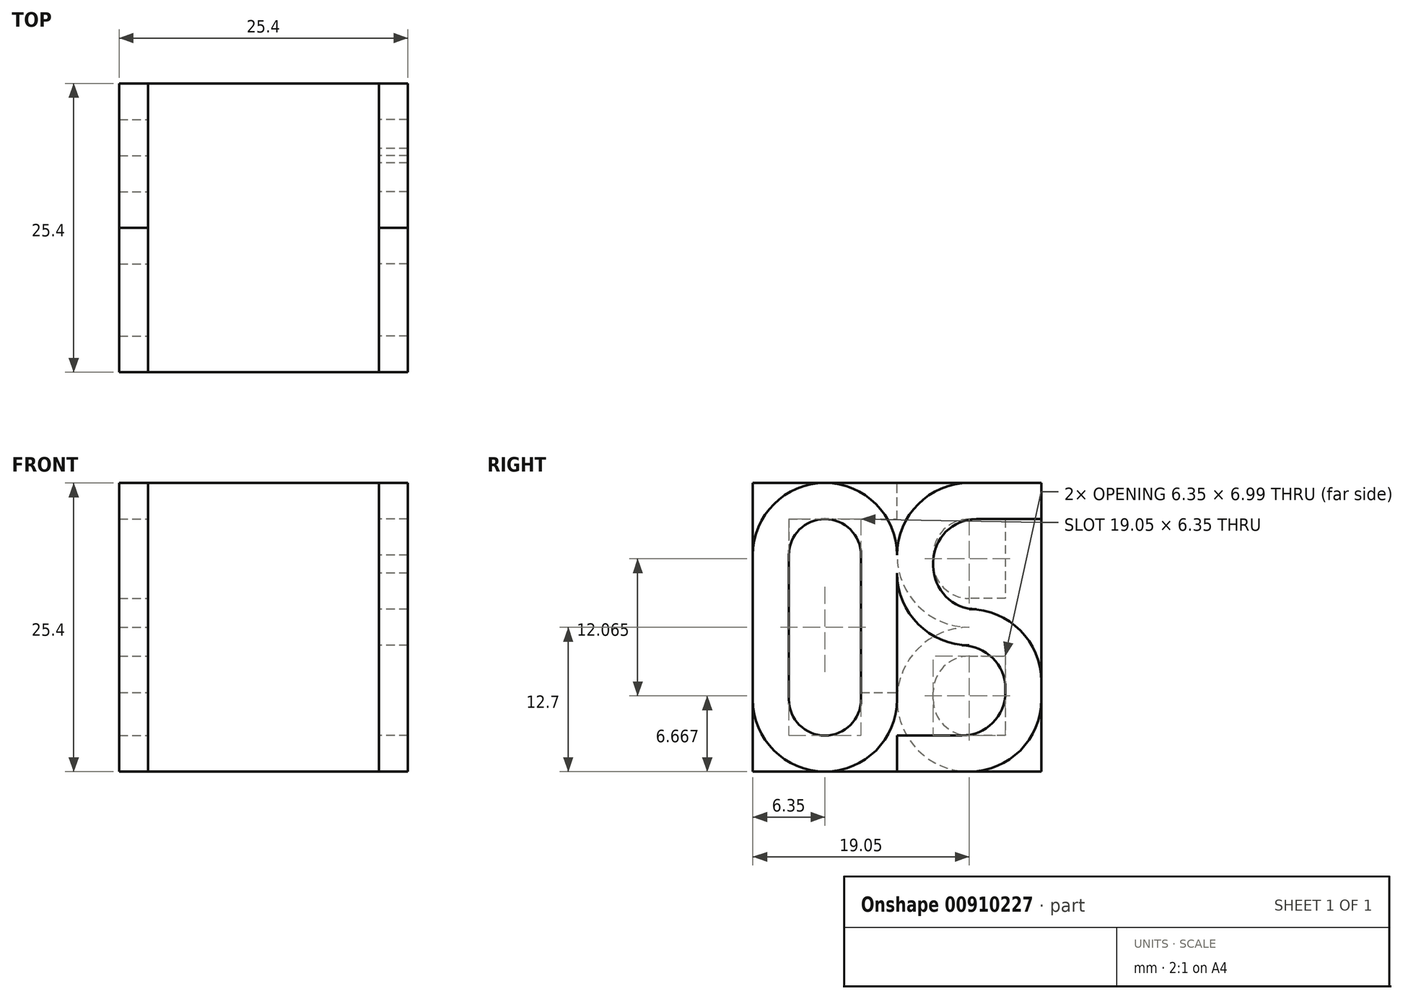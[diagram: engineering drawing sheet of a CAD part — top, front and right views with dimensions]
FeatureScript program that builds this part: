
annotation { "Feature Type Name" : "Feature", "Feature Type Description" : "" }
export const myFeature = defineFeature(function(context is Context, id is Id, definition is map)
    precondition{}
    {
        {
            var Q0;
            Q0=qCreatedBy(makeId("Right.planeOp"),FACE);
            var sketch = newSketch(context, id + "F0", { "sketchPlane" : qUnion([Q0])});
            skLineSegment(sketch, "E0.bottom", {"start": v(11.43, 12.7) * mm, "end": v(6.35, 12.7) * mm});
            skLineSegment(sketch, "E0.top", {"start": v(6.35, -12.7) * mm, "end": v(1.27, -12.7) * mm});
            skLineSegment(sketch, "E0.right", {"start": v(-12.7, 6.35) * mm, "end": v(-12.7, -6.35) * mm});
            skPoint(sketch, "E0.middle", {"position": v(0, 0) * mm});
            skLineSegment(sketch, "E1.bottom", {"start": v(-6.35, 12.7) * mm, "end": v(-6.35, 12.7) * mm});
            skLineSegment(sketch, "E1.right", {"start": v(0, 6.35) * mm, "end": v(0, 4.76) * mm});
            skLineSegment(sketch, "E2.bottom", {"start": v(-6.35, 9.53) * mm, "end": v(-6.35, 9.53) * mm});
            skLineSegment(sketch, "E2.top", {"start": v(-6.35, -9.53) * mm, "end": v(-6.35, -9.53) * mm});
            skLineSegment(sketch, "E2.left", {"start": v(-3.17, 6.35) * mm, "end": v(-3.17, -6.35) * mm});
            skLineSegment(sketch, "E2.right", {"start": v(-9.53, 6.35) * mm, "end": v(-9.53, -6.35) * mm});
            skLineSegment(sketch, "E3", {"start": v(11.43, 9.53) * mm, "end": v(6.98, 9.53) * mm});
            skLineSegment(sketch, "E4", {"start": v(3.18, 5.71) * mm, "end": v(3.18, 5.4) * mm});
            skLineSegment(sketch, "E5", {"start": v(6.35, 1.59) * mm, "end": v(6.98, 1.59) * mm});
            skLineSegment(sketch, "E6", {"start": v(12.7, -4.76) * mm, "end": v(12.7, -6.35) * mm});
            skLineSegment(sketch, "E7", {"start": v(1.27, -9.52) * mm, "end": v(5.72, -9.52) * mm});
            skLineSegment(sketch, "E8", {"start": v(9.53, -5.72) * mm, "end": v(9.53, -5.4) * mm});
            skLineSegment(sketch, "E9", {"start": v(6.35, -1.59) * mm, "end": v(5.71, -1.59) * mm});
            skPoint(sketch, "E10.visualSharp", {"position": v(12.7, -12.7) * mm});
            skArc(sketch, "E10.filletArc", {"start": v(6.35, -12.7) * mm, "mid": v(10.84, -10.84) * mm, "end": v(12.7, -6.35) * mm});
            skPoint(sketch, "E11.visualSharp", {"position": v(9.53, -9.52) * mm});
            skArc(sketch, "E11.filletArc", {"start": v(5.72, -9.53) * mm, "mid": v(8.4, -8.4) * mm, "end": v(9.53, -5.72) * mm});
            skPoint(sketch, "E12.visualSharp", {"position": v(9.53, -1.59) * mm});
            skArc(sketch, "E12.filletArc", {"start": v(9.52, -5.4) * mm, "mid": v(8.4, -2.7) * mm, "end": v(5.71, -1.59) * mm});
            skPoint(sketch, "E13.visualSharp", {"position": v(12.7, 1.59) * mm});
            skArc(sketch, "E13.filletArc", {"start": v(12.7, -4.76) * mm, "mid": v(10.84, -0.27) * mm, "end": v(6.35, 1.59) * mm});
            skArc(sketch, "E14.filletArc", {"start": v(3.17, 5.4) * mm, "mid": v(4.3, 2.7) * mm, "end": v(6.98, 1.59) * mm});
            skPoint(sketch, "E15.newPointA", {"position": v(0, -1.59) * mm});
            skArc(sketch, "E15.filletArc", {"start": v(0, 4.76) * mm, "mid": v(1.86, 0.27) * mm, "end": v(6.35, -1.59) * mm});
            skPoint(sketch, "E16.visualSharp", {"position": v(3.18, 9.53) * mm});
            skArc(sketch, "E16.filletArc", {"start": v(6.98, 9.52) * mm, "mid": v(4.3, 8.4) * mm, "end": v(3.17, 5.71) * mm});
            skPoint(sketch, "E17.newPointA", {"position": v(-12.7, 12.7) * mm});
            skArc(sketch, "E17.filletArc", {"start": v(6.35, 12.7) * mm, "mid": v(1.86, 10.84) * mm, "end": v(0, 6.35) * mm});
            skLineSegment(sketch, "E18", {"start": v(0, 6.35) * mm, "end": v(0, 6.35) * mm});
            skPoint(sketch, "E19.visualSharp", {"position": v(0, 12.7) * mm});
            skArc(sketch, "E19.filletArc", {"start": v(0, 6.35) * mm, "mid": v(-1.86, 10.84) * mm, "end": v(-6.35, 12.7) * mm});
            skArc(sketch, "E20.filletArc", {"start": v(-6.35, 12.7) * mm, "mid": v(-10.84, 10.84) * mm, "end": v(-12.7, 6.35) * mm});
            skPoint(sketch, "E21.visualSharp", {"position": v(-9.53, 9.52) * mm});
            skArc(sketch, "E21.filletArc", {"start": v(-6.35, 9.53) * mm, "mid": v(-8.6, 8.6) * mm, "end": v(-9.53, 6.35) * mm});
            skPoint(sketch, "E22.visualSharp", {"position": v(-3.18, 9.53) * mm});
            skArc(sketch, "E22.filletArc", {"start": v(-3.18, 6.35) * mm, "mid": v(-4.1, 8.6) * mm, "end": v(-6.35, 9.53) * mm});
            skPoint(sketch, "E23.visualSharp", {"position": v(-9.53, -9.53) * mm});
            skArc(sketch, "E23.filletArc", {"start": v(-9.53, -6.35) * mm, "mid": v(-8.6, -8.6) * mm, "end": v(-6.35, -9.53) * mm});
            skArc(sketch, "E24.filletArc", {"start": v(-6.35, -9.53) * mm, "mid": v(-4.1, -8.6) * mm, "end": v(-3.18, -6.35) * mm});
            skPoint(sketch, "E25.visualSharp", {"position": v(0, -12.7) * mm});
            skPoint(sketch, "E26.visualSharp", {"position": v(-12.7, -12.7) * mm});
            skArc(sketch, "E26.filletArc", {"start": v(-12.7, -6.35) * mm, "mid": v(-10.84, -10.84) * mm, "end": v(-6.35, -12.7) * mm});
            skPoint(sketch, "E27.visualSharp", {"position": v(0, -9.52) * mm});
            skPoint(sketch, "E28.visualSharp", {"position": v(12.7, 12.7) * mm});
            skLineSegment(sketch, "E29", {"start": v(0, -3.81) * mm, "end": v(0, 4.76) * mm});
            skLineSegment(sketch, "E30", {"start": v(1.27, -9.52) * mm, "end": v(0, -9.52) * mm});
            skLineSegment(sketch, "E31", {"start": v(0, -12.7) * mm, "end": v(1.27, -12.7) * mm});
            skLineSegment(sketch, "E32", {"start": v(0, -12.7) * mm, "end": v(0, -9.52) * mm});
            skLineSegment(sketch, "E33", {"start": v(0, -3.81) * mm, "end": v(0, -6.35) * mm});
            skLineSegment(sketch, "E34", {"start": v(-6.35, -12.7) * mm, "end": v(-6.35, -12.7) * mm});
            skArc(sketch, "E35.filletArc", {"start": v(-6.35, -12.7) * mm, "mid": v(-1.86, -10.84) * mm, "end": v(0, -6.35) * mm});
            skLineSegment(sketch, "E36", {"start": v(12.7, 12.7) * mm, "end": v(12.7, 9.53) * mm});
            skLineSegment(sketch, "E37", {"start": v(12.7, 9.53) * mm, "end": v(11.43, 9.53) * mm});
            skLineSegment(sketch, "E38", {"start": v(11.43, 12.7) * mm, "end": v(12.7, 12.7) * mm});
            skSolve(sketch);
        }
        {
            var Q0;
            Q0=qCreatedBy(makeId("Right.planeOp"),FACE);
            cPlane(context, id + "F1", {"entities" : qUnion([Q0]), "cplaneType" : CPlaneType.OFFSET, "offset" : 20.32 * mm, "oppositeDirection" : true, "width" : 152.4 * mm, "height" : 152.4 * mm});
        }
        {
            var Q0;
            Q0=qCreatedBy(id+"F1.planeOp",FACE);
            var sketch = newSketch(context, id + "F2", { "sketchPlane" : qUnion([Q0])});
            skLineSegment(sketch, "E39.left", {"start": v(12.7, 12.7) * mm, "end": v(12.7, -12.7) * mm});
            skLineSegment(sketch, "E39.right", {"start": v(-12.7, 12.7) * mm, "end": v(-12.7, -6.35) * mm});
            skPoint(sketch, "E39.middle", {"position": v(0, 0) * mm});
            skPoint(sketch, "E40.newPointA", {"position": v(0, 12.7) * mm});
            skPoint(sketch, "E40.newPointB", {"position": v(-12.7, 12.7) * mm});
            skLineSegment(sketch, "E41", {"start": v(12.7, 12.7) * mm, "end": v(6.35, 12.7) * mm});
            skLineSegment(sketch, "E42", {"start": v(9.53, 9.53) * mm, "end": v(9.53, 2.54) * mm});
            skLineSegment(sketch, "E43", {"start": v(9.53, -9.53) * mm, "end": v(6.35, -9.53) * mm});
            skLineSegment(sketch, "E44", {"start": v(3.18, -6.35) * mm, "end": v(3.18, -5.71) * mm});
            skLineSegment(sketch, "E45", {"start": v(6.35, -2.54) * mm, "end": v(9.53, -2.54) * mm});
            skLineSegment(sketch, "E46", {"start": v(9.53, 2.54) * mm, "end": v(6.35, 2.54) * mm});
            skLineSegment(sketch, "E47", {"start": v(3.18, 5.72) * mm, "end": v(3.18, 6.35) * mm});
            skLineSegment(sketch, "E48.trimOffspring", {"start": v(9.53, -2.54) * mm, "end": v(9.53, -9.53) * mm});
            skLineSegment(sketch, "E49", {"start": v(0, 6.35) * mm, "end": v(0, 6.35) * mm});
            skLineSegment(sketch, "E50", {"start": v(-9.52, 9.52) * mm, "end": v(-9.52, -6.35) * mm});
            skLineSegment(sketch, "E51", {"start": v(-6.35, -9.53) * mm, "end": v(-6.35, -9.53) * mm});
            skLineSegment(sketch, "E52", {"start": v(-3.17, -6.35) * mm, "end": v(-3.17, -5.75) * mm});
            skLineSegment(sketch, "E53", {"start": v(-3.17, -5.75) * mm, "end": v(0, -5.75) * mm});
            skPoint(sketch, "E54.newPointA", {"position": v(-12.7, -12.7) * mm});
            skPoint(sketch, "E54.newPointB", {"position": v(0, -12.7) * mm});
            skArc(sketch, "E54.filletArc", {"start": v(0, -6.35) * mm, "mid": v(1.86, -10.84) * mm, "end": v(6.35, -12.7) * mm});
            skPoint(sketch, "E55.visualSharp", {"position": v(3.18, -2.54) * mm});
            skArc(sketch, "E55.filletArc", {"start": v(6.35, -2.54) * mm, "mid": v(4.1, -3.47) * mm, "end": v(3.18, -5.71) * mm});
            skPoint(sketch, "E56.visualSharp", {"position": v(3.18, -9.53) * mm});
            skArc(sketch, "E56.filletArc", {"start": v(3.18, -6.35) * mm, "mid": v(4.1, -8.6) * mm, "end": v(6.35, -9.53) * mm});
            skPoint(sketch, "E57.visualSharp", {"position": v(3.18, 2.54) * mm});
            skArc(sketch, "E57.filletArc", {"start": v(3.18, 5.72) * mm, "mid": v(4.1, 3.47) * mm, "end": v(6.35, 2.54) * mm});
            skLineSegment(sketch, "E58", {"start": v(0, -6.35) * mm, "end": v(0, -6.35) * mm});
            skLineSegment(sketch, "E59", {"start": v(0, 12.7) * mm, "end": v(-12.7, 12.7) * mm});
            skLineSegment(sketch, "E60", {"start": v(-6.35, -12.7) * mm, "end": v(-6.35, -12.7) * mm});
            skLineSegment(sketch, "E61", {"start": v(0, -6.35) * mm, "end": v(0, -5.75) * mm});
            skLineSegment(sketch, "E62", {"start": v(6.35, 0) * mm, "end": v(6.35, 0) * mm});
            skArc(sketch, "E63.filletArc", {"start": v(6.35, 0) * mm, "mid": v(1.86, -1.86) * mm, "end": v(0, -6.35) * mm});
            skPoint(sketch, "E64.visualSharp", {"position": v(-9.52, -9.53) * mm});
            skArc(sketch, "E64.filletArc", {"start": v(-9.52, -6.35) * mm, "mid": v(-8.6, -8.6) * mm, "end": v(-6.35, -9.53) * mm});
            skPoint(sketch, "E65.visualSharp", {"position": v(-3.17, -9.53) * mm});
            skArc(sketch, "E65.filletArc", {"start": v(-6.35, -9.53) * mm, "mid": v(-4.1, -8.6) * mm, "end": v(-3.17, -6.35) * mm});
            skArc(sketch, "E66.filletArc", {"start": v(-6.35, -12.7) * mm, "mid": v(-1.86, -10.84) * mm, "end": v(0, -6.35) * mm});
            skArc(sketch, "E67.filletArc", {"start": v(-12.7, -6.35) * mm, "mid": v(-10.84, -10.84) * mm, "end": v(-6.35, -12.7) * mm});
            skPoint(sketch, "E68.end.orphan", {"position": v(12.7, 0) * mm});
            skLineSegment(sketch, "E69.bottom", {"start": v(12.7, -12.7) * mm, "end": v(6.35, -12.7) * mm});
            skLineSegment(sketch, "E69.left", {"start": v(12.7, -12.7) * mm, "end": v(12.7, 12.7) * mm});
            skLineSegment(sketch, "E69.right", {"start": v(-12.7, -6.35) * mm, "end": v(-12.7, 12.7) * mm});
            skPoint(sketch, "E70.start.orphan", {"position": v(0, 9.53) * mm});
            skLineSegment(sketch, "E71", {"start": v(9.53, 9.53) * mm, "end": v(6.35, 9.53) * mm});
            skLineSegment(sketch, "E72", {"start": v(3.18, 6.35) * mm, "end": v(3.18, 6.35) * mm});
            skPoint(sketch, "E73.visualSharp", {"position": v(3.18, 9.53) * mm});
            skArc(sketch, "E73.filletArc", {"start": v(6.35, 9.53) * mm, "mid": v(4.1, 8.6) * mm, "end": v(3.18, 6.35) * mm});
            skLineSegment(sketch, "E74", {"start": v(-9.52, 9.52) * mm, "end": v(0, 9.53) * mm});
            skLineSegment(sketch, "E75", {"start": v(0, 9.53) * mm, "end": v(0, 12.7) * mm});
            skArc(sketch, "E76.filletArc", {"start": v(6.35, 12.7) * mm, "mid": v(1.86, 10.84) * mm, "end": v(0, 6.35) * mm});
            skArc(sketch, "E77.filletArc", {"start": v(0, 6.35) * mm, "mid": v(1.86, 1.86) * mm, "end": v(6.35, 0) * mm});
            skSolve(sketch);
        }
        {
            var Q0;
            Q0=makeQuery(id+"F0.imprint","IMPRINT",FACE,{"disambiguationData":[TD([[makeQuery(id+"F0.imprint","IMPRINT",EDGE,{"derivedFrom":sQuery(id+"F0.wireOp",EDGE,"E1.right")}),-1.0]])]});
            var Q1;
            Q1=makeQuery(id+"F0.imprint","IMPRINT",FACE,{"disambiguationData":[TD([[makeQuery(id+"F0.imprint","IMPRINT",EDGE,{"derivedFrom":sQuery(id+"F0.wireOp",EDGE,"E1.right")}),1.0]])]});
            extrude(context, id + "F3", {"entities" : qUnion([Q0, Q1]), "depth" : 2.54 * mm, "offsetDistance" : 25.4 * mm});
        }
        {
            var Q0;
            Q0=makeQuery(id+"F2.imprint","IMPRINT",FACE,{"disambiguationData":[TD([[makeQuery(id+"F2.imprint","IMPRINT",EDGE,{"derivedFrom":sQuery(id+"F2.wireOp",EDGE,"E42")}),1.0]])]});
            var Q1;
            Q1=makeQuery(id+"F2.imprint","IMPRINT",FACE,{"disambiguationData":[TD([[makeQuery(id+"F2.imprint","IMPRINT",EDGE,{"derivedFrom":sQuery(id+"F2.wireOp",EDGE,"E50")}),-1.0]])]});
            extrude(context, id + "F4", {"entities" : qUnion([Q0, Q1]), "oppositeDirection" : true, "depth" : 2.54 * mm, "offsetDistance" : 25.4 * mm});
        }
        {
            var Q0;
            Q0=makeQuery(id+"F4.opExtrude","CAP_FACE",FACE,{"disambiguationData":[OSD([sQuery(id+"F2.wireOp",EDGE,"E42"),sQuery(id+"F2.wireOp",EDGE,"E43"),sQuery(id+"F2.wireOp",EDGE,"E44"),sQuery(id+"F2.wireOp",EDGE,"E45"),sQuery(id+"F2.wireOp",EDGE,"E46"),sQuery(id+"F2.wireOp",EDGE,"E47"),sQuery(id+"F2.wireOp",EDGE,"E48.trimOffspring"),sQuery(id+"F2.wireOp",EDGE,"E54.filletArc"),sQuery(id+"F2.wireOp",EDGE,"E55.filletArc"),sQuery(id+"F2.wireOp",EDGE,"E56.filletArc"),sQuery(id+"F2.wireOp",EDGE,"E57.filletArc"),sQuery(id+"F2.wireOp",EDGE,"E63.filletArc"),sQuery(id+"F2.wireOp",EDGE,"E69.bottom"),sQuery(id+"F2.wireOp",EDGE,"E41"),sQuery(id+"F2.wireOp",EDGE,"E69.left"),sQuery(id+"F2.wireOp",EDGE,"E71"),sQuery(id+"F2.wireOp",EDGE,"E73.filletArc"),sQuery(id+"F2.wireOp",EDGE,"E76.filletArc"),sQuery(id+"F2.wireOp",EDGE,"E77.filletArc")])],"isStart":true});
            var sketch = newSketch(context, id + "F5", { "sketchPlane" : qUnion([Q0])});
            skLineSegment(sketch, "E78.bottom", {"start": v(-12.7, -12.7) * mm, "end": v(12.7, -12.7) * mm});
            skLineSegment(sketch, "E78.top", {"start": v(-12.7, 12.7) * mm, "end": v(12.7, 12.7) * mm});
            skLineSegment(sketch, "E78.left", {"start": v(-12.7, -12.7) * mm, "end": v(-12.7, 12.7) * mm});
            skLineSegment(sketch, "E78.right", {"start": v(12.7, -12.7) * mm, "end": v(12.7, 12.7) * mm});
            skPoint(sketch, "E78.middle", {"position": v(0, 0) * mm});
            skSolve(sketch);
        }
        {
            var Q0;
            Q0 = qSketchRegion(id + "F5", true);
            extrude(context, id + "F6", {"entities" : qUnion([Q0]), "depth" : 20.32 * mm, "offsetDistance" : 25.4 * mm});
        }
    });
